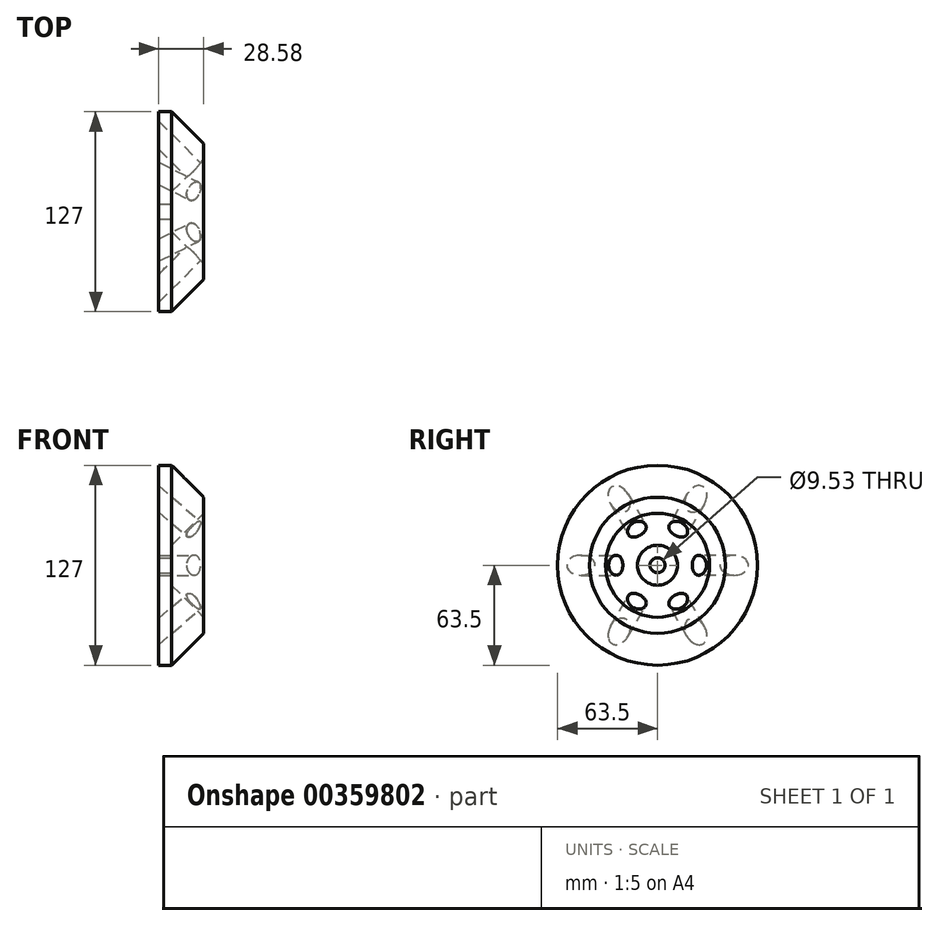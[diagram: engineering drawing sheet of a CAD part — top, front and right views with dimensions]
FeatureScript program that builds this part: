
annotation { "Feature Type Name" : "Feature", "Feature Type Description" : "" }
export const myFeature = defineFeature(function(context is Context, id is Id, definition is map)
    precondition{}
    {
        {
            var Q0;
            Q0=qCreatedBy(makeId("Front.planeOp"),FACE);
            var sketch = newSketch(context, id + "F0", { "sketchPlane" : qUnion([Q0])});
            skLineSegment(sketch, "E0", {"start": v(0, 0) * mm, "end": v(0, 12.7) * mm});
            skLineSegment(sketch, "E1", {"start": v(0, 12.7) * mm, "end": v(20.32, 33.02) * mm});
            skLineSegment(sketch, "E2", {"start": v(20.32, 33.02) * mm, "end": v(20.32, 43.18) * mm});
            skLineSegment(sketch, "E3", {"start": v(20.32, 43.18) * mm, "end": v(0, 63.5) * mm});
            skLineSegment(sketch, "E4", {"start": v(0, 63.5) * mm, "end": v(-8.26, 63.5) * mm});
            skLineSegment(sketch, "E5", {"start": v(-8.26, 63.5) * mm, "end": v(-8.26, 0) * mm});
            skLineSegment(sketch, "E6", {"start": v(-8.25, 0) * mm, "end": v(0, 0) * mm});
            skSolve(sketch);
        }
        {
            var Q0;
            Q0=makeQuery(id+"F0.imprint","IMPRINT",FACE,{"disambiguationData":[TD([[makeQuery(id+"F0.imprint","IMPRINT",EDGE,{"derivedFrom":sQuery(id+"F0.wireOp",EDGE,"E0")}),1.0]])]});
            var Q1;
            Q1=sQuery(id+"F0.wireOp",EDGE,"E6");
            revolve(context, id + "F1", {"entities" : qUnion([Q0]), "axis" : qUnion([Q1]), "revolveType" : RevolveType.FULL});
        }
        {
            var Q0;
            Q0=qCreatedBy(makeId("Right.planeOp"),FACE);
            var sketch = newSketch(context, id + "F2", { "sketchPlane" : qUnion([Q0])});
            skLineSegment(sketch, "E7", {"start": v(0, 63.5) * mm, "end": v(0, -63.5) * mm, "construction": true});
            skLineSegment(sketch, "E8.1.0", {"start": v(-55, -31.75) * mm, "end": v(55, 31.75) * mm, "construction": true});
            skLineSegment(sketch, "E8.2.0", {"start": v(55, -31.75) * mm, "end": v(-55, 31.75) * mm, "construction": true});
            skPoint(sketch, "E8.center", {"position": v(0, 0) * mm});
            skSolve(sketch);
        }
        {
            var Q0;
            Q0=sQuery(id+"F2.wireOp",EDGE,"E8.1.0");
            cPlane(context, id + "F3", {"entities" : qUnion([Q0]), "cplaneType" : CPlaneType.LINE_ANGLE, "offset" : 25.4 * mm, "angle" : 45 * degree, "width" : 152.4 * mm, "height" : 152.4 * mm});
        }
        {
            var Q0;
            Q0=sQuery(id+"F2.wireOp",EDGE,"E8.1.0");
            cPlane(context, id + "F4", {"entities" : qUnion([Q0]), "cplaneType" : CPlaneType.LINE_ANGLE, "offset" : 25.4 * mm, "angle" : 135 * degree, "width" : 152.4 * mm, "height" : 152.4 * mm});
        }
        {
            var Q0;
            Q0=sQuery(id+"F2.wireOp",EDGE,"E8.2.0");
            cPlane(context, id + "F5", {"entities" : qUnion([Q0]), "cplaneType" : CPlaneType.LINE_ANGLE, "offset" : 25.4 * mm, "angle" : 45 * degree, "width" : 152.4 * mm, "height" : 152.4 * mm});
        }
        {
            var Q0;
            Q0=sQuery(id+"F2.wireOp",EDGE,"E8.2.0");
            cPlane(context, id + "F6", {"entities" : qUnion([Q0]), "cplaneType" : CPlaneType.LINE_ANGLE, "offset" : 25.4 * mm, "angle" : 135 * degree, "width" : 152.4 * mm, "height" : 152.4 * mm});
        }
        {
            var Q0;
            Q0=sQuery(id+"F2.wireOp",EDGE,"E7");
            cPlane(context, id + "F7", {"entities" : qUnion([Q0]), "cplaneType" : CPlaneType.LINE_ANGLE, "offset" : 25.4 * mm, "angle" : 45 * degree, "width" : 152.4 * mm, "height" : 152.4 * mm});
        }
        {
            var Q0;
            Q0=sQuery(id+"F2.wireOp",EDGE,"E7");
            cPlane(context, id + "F8", {"entities" : qUnion([Q0]), "cplaneType" : CPlaneType.LINE_ANGLE, "offset" : 25.4 * mm, "angle" : 135 * degree, "width" : 152.4 * mm, "height" : 152.4 * mm});
        }
        {
            var Q0;
            Q0=qCreatedBy(id+"F3.planeOp",FACE);
            var sketch = newSketch(context, id + "F9", { "sketchPlane" : qUnion([Q0])});
            skCircle(sketch, "E9", {"center": v(10.8, -26.46) * mm, "radius": 6.35 * mm});
            skLineSegment(sketch, "E10", {"start": v(10.8, -26.46) * mm, "end": v(0, 0) * mm, "construction": true});
            skSolve(sketch);
        }
        {
            var Q0;
            Q0=qCreatedBy(id+"F4.planeOp",FACE);
            var sketch = newSketch(context, id + "F10", { "sketchPlane" : qUnion([Q0])});
            skCircle(sketch, "E11", {"center": v(-10.8, 26.46) * mm, "radius": 6.35 * mm});
            skLineSegment(sketch, "E12", {"start": v(0, 0) * mm, "end": v(-10.8, 26.46) * mm, "construction": true});
            skSolve(sketch);
        }
        {
            var Q0;
            Q0=qCreatedBy(id+"F5.planeOp",FACE);
            var sketch = newSketch(context, id + "F11", { "sketchPlane" : qUnion([Q0])});
            skCircle(sketch, "E13", {"center": v(10.8, 26.46) * mm, "radius": 6.35 * mm});
            skLineSegment(sketch, "E14", {"start": v(10.8, 26.46) * mm, "end": v(0, 0) * mm, "construction": true});
            skSolve(sketch);
        }
        {
            var Q0;
            Q0=qCreatedBy(id+"F6.planeOp",FACE);
            var sketch = newSketch(context, id + "F12", { "sketchPlane" : qUnion([Q0])});
            skCircle(sketch, "E15", {"center": v(-10.8, -26.46) * mm, "radius": 6.35 * mm});
            skLineSegment(sketch, "E16", {"start": v(0, 0) * mm, "end": v(-10.8, -26.46) * mm, "construction": true});
            skSolve(sketch);
        }
        {
            var Q0;
            Q0=qCreatedBy(id+"F7.planeOp",FACE);
            var sketch = newSketch(context, id + "F13", { "sketchPlane" : qUnion([Q0])});
            skCircle(sketch, "E17", {"center": v(-28.58, 0) * mm, "radius": 6.35 * mm});
            skLineSegment(sketch, "E18", {"start": v(-28.58, 0) * mm, "end": v(0, 0) * mm, "construction": true});
            skSolve(sketch);
        }
        {
            var Q0;
            Q0=qCreatedBy(id+"F8.planeOp",FACE);
            var sketch = newSketch(context, id + "F14", { "sketchPlane" : qUnion([Q0])});
            skCircle(sketch, "E19", {"center": v(-28.58, 0) * mm, "radius": 6.35 * mm});
            skLineSegment(sketch, "E20", {"start": v(-28.58, 0) * mm, "end": v(0, 0) * mm, "construction": true});
            skSolve(sketch);
        }
        {
            var Q0;
            Q0=makeQuery(id+"F10.imprint","IMPRINT",FACE,{"disambiguationData":[TD([[makeQuery(id+"F10.imprint","IMPRINT",EDGE,{"derivedFrom":sQuery(id+"F10.wireOp",EDGE,"E11")}),1.0]])]});
            extrude(context, id + "F15", {"entities" : qUnion([Q0]), "operationType" : NewBodyOperationType.REMOVE, "endBound" : BoundingType.THROUGH_ALL, "oppositeDirection" : true, "depth" : 25.4 * mm});
        }
        {
            var Q0;
            Q0=makeQuery(id+"F11.imprint","IMPRINT",FACE,{"disambiguationData":[TD([[makeQuery(id+"F11.imprint","IMPRINT",EDGE,{"derivedFrom":sQuery(id+"F11.wireOp",EDGE,"E13")}),1.0]])]});
            extrude(context, id + "F16", {"entities" : qUnion([Q0]), "operationType" : NewBodyOperationType.REMOVE, "endBound" : BoundingType.THROUGH_ALL, "oppositeDirection" : true, "depth" : 25.4 * mm});
        }
        {
            var Q0;
            Q0=makeQuery(id+"F14.imprint","IMPRINT",FACE,{"disambiguationData":[TD([[makeQuery(id+"F14.imprint","IMPRINT",EDGE,{"derivedFrom":sQuery(id+"F14.wireOp",EDGE,"E19")}),1.0]])]});
            extrude(context, id + "F17", {"entities" : qUnion([Q0]), "operationType" : NewBodyOperationType.REMOVE, "endBound" : BoundingType.THROUGH_ALL, "oppositeDirection" : true, "depth" : 25.4 * mm});
        }
        {
            var Q0;
            Q0=makeQuery(id+"F13.imprint","IMPRINT",FACE,{"disambiguationData":[TD([[makeQuery(id+"F13.imprint","IMPRINT",EDGE,{"derivedFrom":sQuery(id+"F13.wireOp",EDGE,"E17")}),1.0]])]});
            extrude(context, id + "F18", {"entities" : qUnion([Q0]), "operationType" : NewBodyOperationType.REMOVE, "endBound" : BoundingType.THROUGH_ALL, "depth" : 25.4 * mm});
        }
        {
            var Q0;
            Q0=makeQuery(id+"F9.imprint","IMPRINT",FACE,{"disambiguationData":[TD([[makeQuery(id+"F9.imprint","IMPRINT",EDGE,{"derivedFrom":sQuery(id+"F9.wireOp",EDGE,"E9")}),1.0]])]});
            var Q1;
            Q1=sQuery(id+"F9.wireOp",EDGE,"E9");
            extrude(context, id + "F19", {"entities" : qUnion([Q0]), "operationType" : NewBodyOperationType.REMOVE, "surfaceEntities" : qUnion([Q1]), "endBound" : BoundingType.THROUGH_ALL, "oppositeDirection" : true, "depth" : 25.4 * mm});
        }
        {
            var Q0;
            Q0=makeQuery(id+"F12.imprint","IMPRINT",FACE,{"disambiguationData":[TD([[makeQuery(id+"F12.imprint","IMPRINT",EDGE,{"derivedFrom":sQuery(id+"F12.wireOp",EDGE,"E15")}),1.0]])]});
            extrude(context, id + "F20", {"entities" : qUnion([Q0]), "operationType" : NewBodyOperationType.REMOVE, "endBound" : BoundingType.THROUGH_ALL, "oppositeDirection" : true, "depth" : 25.4 * mm});
        }
        {
            var Q0;
            Q0=sQuery(id+"F2.wireOp",VERTEX,"E8.center");
            var Q1;
            Q1=makeQuery(id+"F1.opRevolve","SWEPT_BODY",BODY,{"disambiguationData":[OSD([sQuery(id+"F0.wireOp",EDGE,"E0"),sQuery(id+"F0.wireOp",EDGE,"E1"),sQuery(id+"F0.wireOp",EDGE,"E2"),sQuery(id+"F0.wireOp",EDGE,"E3"),sQuery(id+"F0.wireOp",EDGE,"E4"),sQuery(id+"F0.wireOp",EDGE,"E5"),sQuery(id+"F0.wireOp",EDGE,"E6")])]});
            hole(context, id + "F21", {"style" : HoleStyle.SIMPLE, "endStyle" : HoleEndStyle.THROUGH, "holeDiameter" : 9.52 * mm, "isTappedThrough" : true, "tappedDepth" : 12.7 * mm, "tapClearance" : 3, "locations" : qUnion([Q0]), "scope" : qUnion([Q1])});
        }
    });
